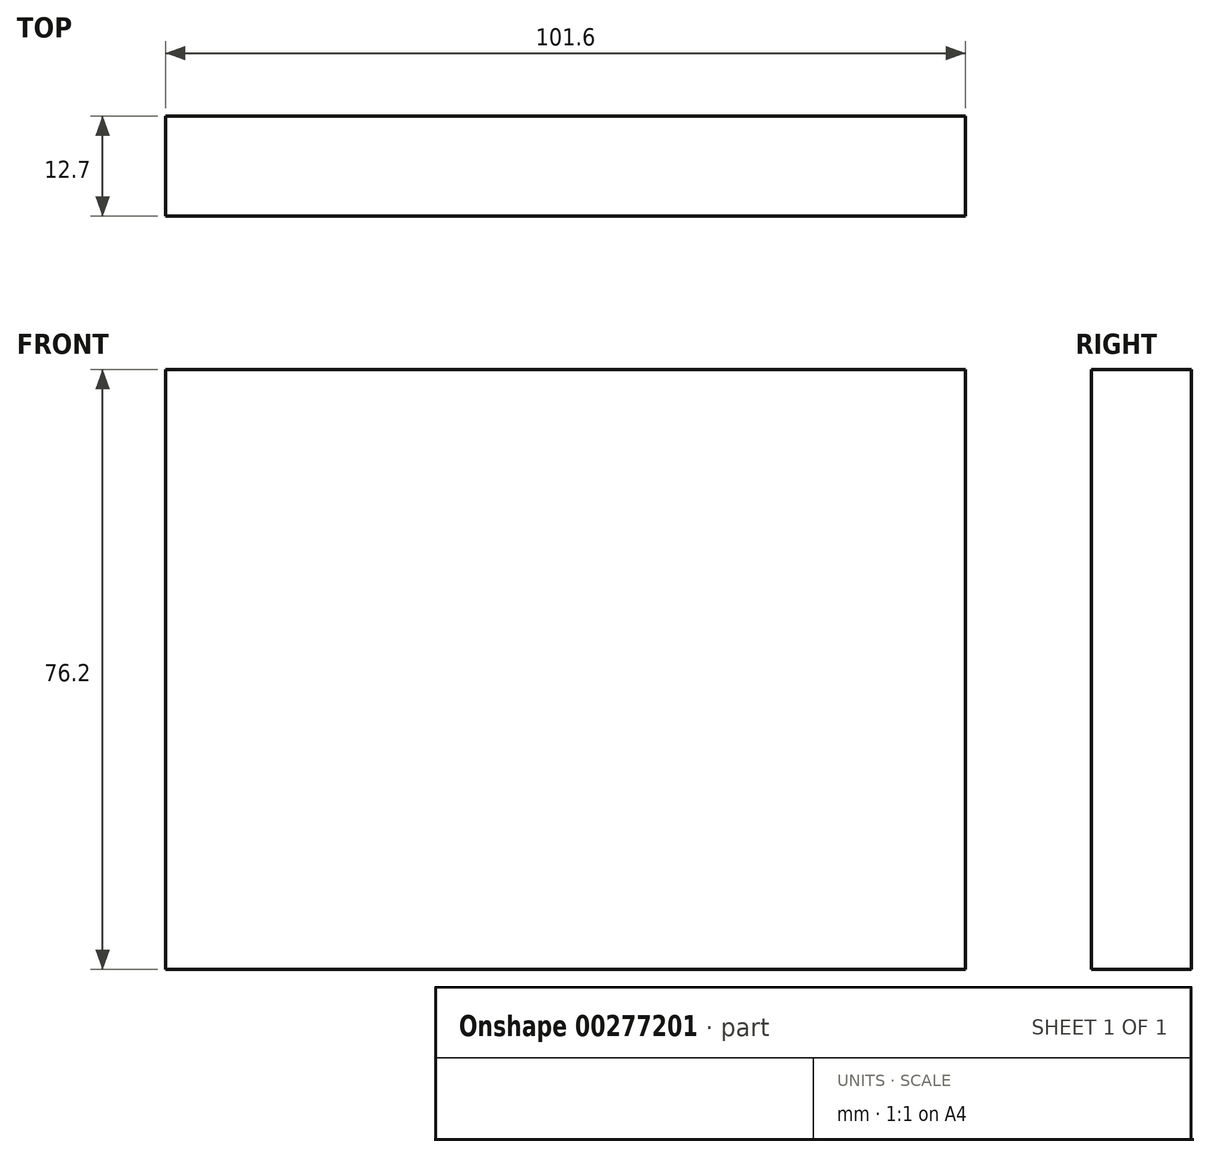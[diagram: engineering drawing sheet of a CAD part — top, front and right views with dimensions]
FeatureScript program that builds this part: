
annotation { "Feature Type Name" : "Feature", "Feature Type Description" : "" }
export const myFeature = defineFeature(function(context is Context, id is Id, definition is map)
    precondition{}
    {
        {
            var Q0;
            Q0=qCreatedBy(makeId("Front.planeOp"),FACE);
            var sketch = newSketch(context, id + "F0", { "sketchPlane" : qUnion([Q0])});
            skPoint(sketch, "E0.middle", {"position": v(0, 0) * mm});
            skLineSegment(sketch, "E1.bottom", {"start": v(0, 0) * mm, "end": v(101.6, 0) * mm});
            skLineSegment(sketch, "E1.top", {"start": v(0, 76.2) * mm, "end": v(101.6, 76.2) * mm});
            skLineSegment(sketch, "E1.left", {"start": v(0, 0) * mm, "end": v(0, 76.2) * mm});
            skLineSegment(sketch, "E1.right", {"start": v(101.6, 0) * mm, "end": v(101.6, 76.2) * mm});
            skArc(sketch, "E2", {"start": v(25.4, 0) * mm, "mid": v(47.72, 53.88) * mm, "end": v(101.6, 76.2) * mm});
            skSolve(sketch);
        }
        {
            var Q0;
            Q0=makeQuery(id+"F0.imprint","IMPRINT",FACE,{"disambiguationData":[TD([[makeQuery(id+"F0.imprint","IMPRINT",EDGE,{"derivedFrom":sQuery(id+"F0.wireOp",EDGE,"E1.top")}),-1.0]])]});
            var Q1;
            {var subQ0=sQuery(id+"F0.wireOp",EDGE,"E1.right");Q1=makeQuery(id+"F0.imprint","IMPRINT",FACE,{"disambiguationData":[TD([[makeQuery(id+"F0.imprint","IMPRINT",EDGE,{"derivedFrom":subQ0}),1.0]])]});}
            extrude(context, id + "F1", {"entities" : qUnion([Q0, Q1]), "oppositeDirection" : true, "depth" : 12.7 * mm});
        }
        {
            var Q0;
            Q0=qCreatedBy(makeId("Top.planeOp"),FACE);
            var sketch = newSketch(context, id + "F2", { "sketchPlane" : qUnion([Q0])});
            skArc(sketch, "E3", {"start": v(45.55, 0) * mm, "mid": v(35.39, -10.16) * mm, "end": v(25.23, 0) * mm});
            skSolve(sketch);
        }
    });
